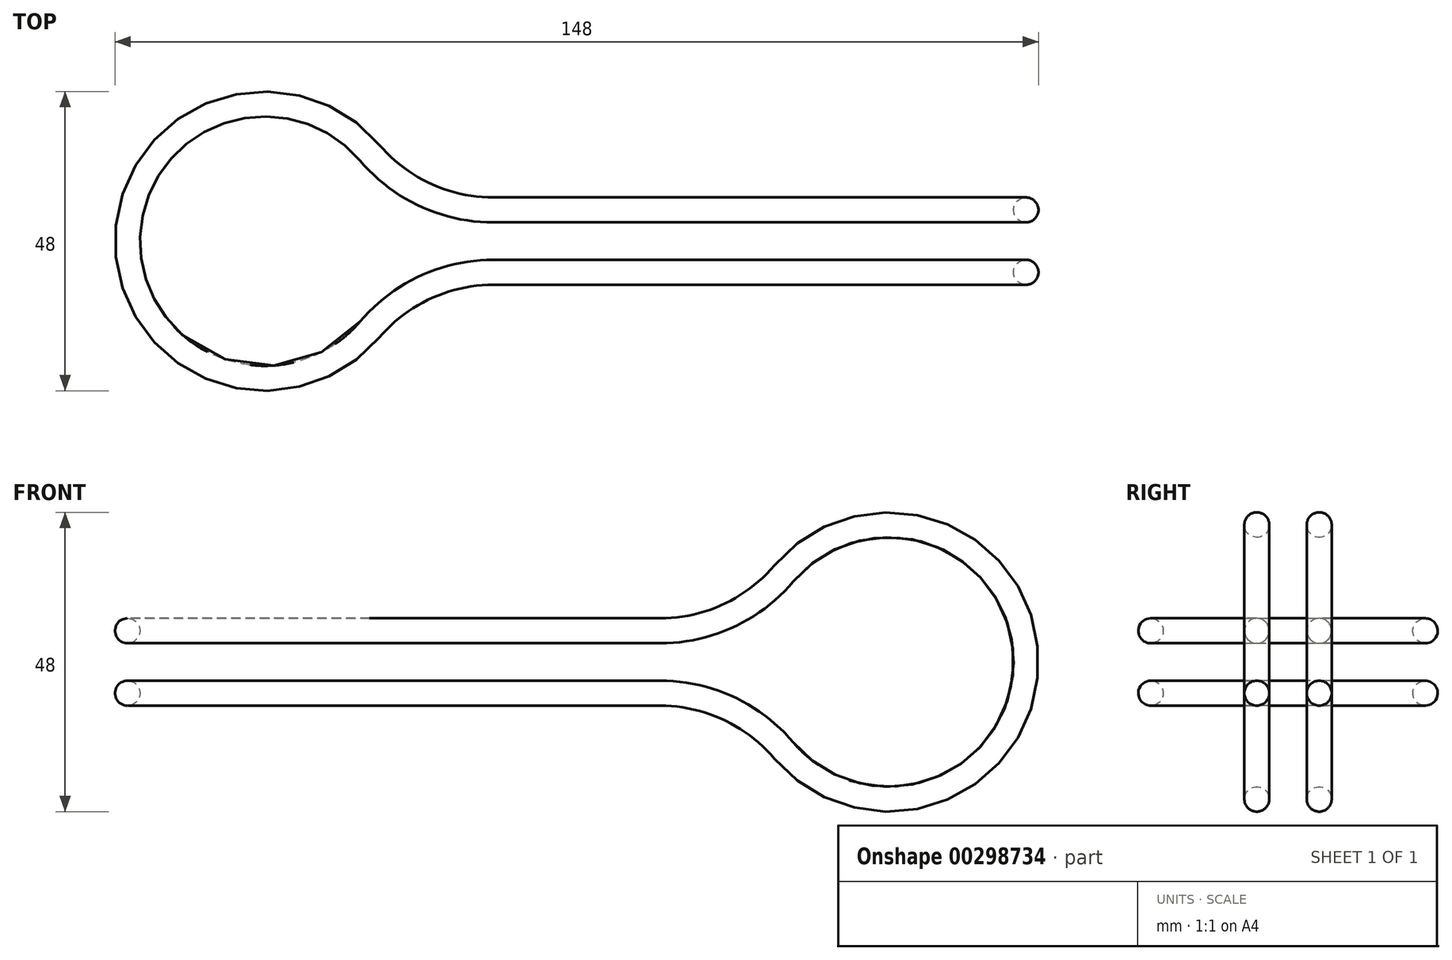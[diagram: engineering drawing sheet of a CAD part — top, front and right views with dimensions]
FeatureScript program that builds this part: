
annotation { "Feature Type Name" : "Feature", "Feature Type Description" : "" }
export const myFeature = defineFeature(function(context is Context, id is Id, definition is map)
    precondition{}
    {
        {
            assignVariable(context, id + "F0", {"name" : "odstup", "anyValue" : 10});
        }
        {
            var Q0;
            Q0=qCreatedBy(makeId("Front.planeOp"),FACE);
            cPlane(context, id + "F1", {"entities" : qUnion([Q0]), "cplaneType" : CPlaneType.OFFSET, "offset" : (getVariable(context, 'odstup') / 2) * mm, "width" : 150 * mm, "height" : 150 * mm});
        }
        {
            var Q0;
            Q0=qCreatedBy(makeId("Top.planeOp"),FACE);
            cPlane(context, id + "F2", {"entities" : qUnion([Q0]), "cplaneType" : CPlaneType.OFFSET, "offset" : (getVariable(context, 'odstup') / 2) * mm, "width" : 150 * mm, "height" : 150 * mm});
        }
        {
            var Q0;
            Q0=qCreatedBy(id+"F1.planeOp",FACE);
            var sketch = newSketch(context, id + "F3", { "sketchPlane" : qUnion([Q0])});
            skLineSegment(sketch, "E0", {"start": v(0, 5) * mm, "end": v(13.35, 5) * mm});
            skArc(sketch, "E1", {"start": v(33.2, 14.2) * mm, "mid": v(57.57, 20.66) * mm, "end": v(72, 0) * mm});
            skPoint(sketch, "E2.visualSharp", {"position": v(28.58, 5) * mm});
            skArc(sketch, "E2.filletArc", {"start": v(13.35, 5) * mm, "mid": v(24.3, 7.41) * mm, "end": v(33.2, 14.2) * mm});
            skSolve(sketch);
        }
        {
            var Q0;
            Q0=qCreatedBy(id+"F2.planeOp",FACE);
            var sketch = newSketch(context, id + "F4", { "sketchPlane" : qUnion([Q0])});
            skLineSegment(sketch, "E3", {"start": v(0, -5) * mm, "end": v(-13.35, -5) * mm});
            skArc(sketch, "E4", {"start": v(-33.2, -14.2) * mm, "mid": v(-57.57, -20.66) * mm, "end": v(-72, 0) * mm});
            skPoint(sketch, "E5.visualSharp", {"position": v(-28.58, -5) * mm});
            skArc(sketch, "E5.filletArc", {"start": v(-13.35, -5) * mm, "mid": v(-24.3, -7.41) * mm, "end": v(-33.2, -14.2) * mm});
            skSolve(sketch);
        }
        {
            var Q0;
            Q0=qCreatedBy(makeId("Top.planeOp"),FACE);
            var sketch = newSketch(context, id + "F5", { "sketchPlane" : qUnion([Q0])});
            skPoint(sketch, "E6.0", {"position": v(72, -5) * mm});
            skCircle(sketch, "E7", {"center": v(72, -5) * mm, "radius": 2 * mm});
            skSolve(sketch);
        }
        {
            var Q0;
            Q0=makeQuery(id+"F5.imprint","IMPRINT",FACE,{"disambiguationData":[TD([[makeQuery(id+"F5.imprint","IMPRINT",EDGE,{"derivedFrom":sQuery(id+"F5.wireOp",EDGE,"E7")}),1.0]])]});
            var Q1;
            Q1=sQuery(id+"F3.wireOp",EDGE,"E1");
            var Q2;
            Q2=sQuery(id+"F3.wireOp",EDGE,"E2.filletArc");
            var Q3;
            Q3=sQuery(id+"F3.wireOp",EDGE,"E0");
            var Q4;
            Q4=sQuery(id+"F4.wireOp",EDGE,"E3");
            var Q5;
            Q5=sQuery(id+"F4.wireOp",EDGE,"E5.filletArc");
            var Q6;
            Q6=sQuery(id+"F4.wireOp",EDGE,"E4");
            sweep(context, id + "F6", {"profiles" : qUnion([Q0]), "path" : qUnion([Q1, Q2, Q3, Q4, Q5, Q6])});
        }
        {
            var Q0;
            Q0=makeQuery(id+"F6.opSweep","SWEPT_BODY",BODY,{"disambiguationData":[OSD([sQuery(id+"F4.wireOp",EDGE,"E4"),sQuery(id+"F5.wireOp",EDGE,"E7")])]});
            var Q1;
            Q1=qCreatedBy(makeId("Front.planeOp"),FACE);
            mirror(context, id + "F7", {"operationType" : NewBodyOperationType.ADD, "entities" : qUnion([Q0]), "mirrorPlane" : qUnion([Q1])});
        }
        {
            var Q0;
            Q0=makeQuery(id+"F6.opSweep","SWEPT_BODY",BODY,{"disambiguationData":[OSD([sQuery(id+"F4.wireOp",EDGE,"E4"),sQuery(id+"F5.wireOp",EDGE,"E7")])]});
            var Q1;
            Q1=qCreatedBy(makeId("Top.planeOp"),FACE);
            mirror(context, id + "F8", {"operationType" : NewBodyOperationType.ADD, "entities" : qUnion([Q0]), "mirrorPlane" : qUnion([Q1])});
        }
    });
